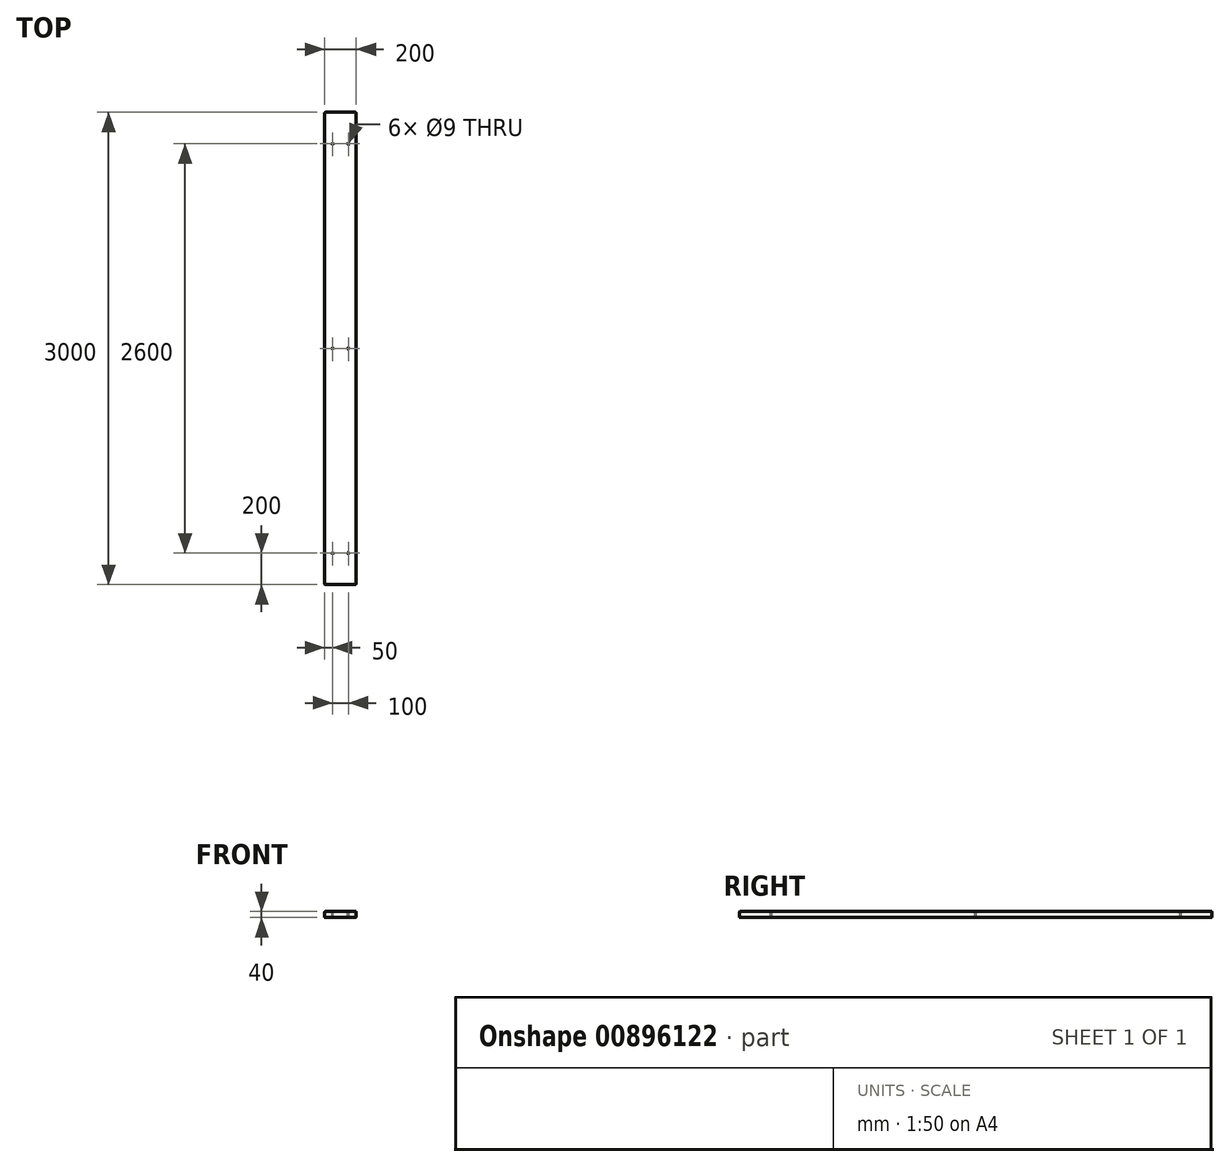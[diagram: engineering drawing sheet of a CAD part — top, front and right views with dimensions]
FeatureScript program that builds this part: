
annotation { "Feature Type Name" : "Feature", "Feature Type Description" : "" }
export const myFeature = defineFeature(function(context is Context, id is Id, definition is map)
    precondition{}
    {
        {
            var Q0;
            Q0=qCreatedBy(makeId("Front.planeOp"),FACE);
            var sketch = newSketch(context, id + "F0", { "sketchPlane" : qUnion([Q0])});
            skLineSegment(sketch, "E0.bottom", {"start": v(0, 0) * mm, "end": v(200, 0) * mm});
            skLineSegment(sketch, "E0.top", {"start": v(0, 40) * mm, "end": v(200, 40) * mm});
            skLineSegment(sketch, "E0.left", {"start": v(0, 0) * mm, "end": v(0, 40) * mm});
            skLineSegment(sketch, "E0.right", {"start": v(200, 0) * mm, "end": v(200, 40) * mm});
            skSolve(sketch);
        }
        {
            var Q0;
            Q0=qSketchRegion(id+"F0",true);
            extrude(context, id + "F1", {"entities" : qUnion([Q0]), "depth" : 3000 * mm, "offsetDistance" : 25 * mm});
        }
        {
            var Q0;
            Q0=makeQuery(id+"F1.opExtrude","SWEPT_FACE",FACE,{"disambiguationData":[OSD([sQuery(id+"F0.wireOp",EDGE,"E0.top")])]});
            var sketch = newSketch(context, id + "F2", { "sketchPlane" : qUnion([Q0])});
            skLineSegment(sketch, "E1", {"start": v(0, -3000) * mm, "end": v(50, -3000) * mm, "construction": true});
            skLineSegment(sketch, "E2", {"start": v(50, -3000) * mm, "end": v(150, -3000) * mm, "construction": true});
            skLineSegment(sketch, "E3", {"start": v(150, -3000) * mm, "end": v(200, -3000) * mm, "construction": true});
            skLineSegment(sketch, "E4", {"start": v(50, -3000) * mm, "end": v(50, -2800) * mm, "construction": true});
            skLineSegment(sketch, "E5", {"start": v(50, -2800) * mm, "end": v(50, -200) * mm, "construction": true});
            skLineSegment(sketch, "E6", {"start": v(50, -200) * mm, "end": v(50, 0) * mm, "construction": true});
            skLineSegment(sketch, "E7", {"start": v(150, -3000) * mm, "end": v(150, -2800) * mm, "construction": true});
            skLineSegment(sketch, "E8", {"start": v(150, -2800) * mm, "end": v(150, -200) * mm, "construction": true});
            skLineSegment(sketch, "E9", {"start": v(150, -200) * mm, "end": v(150, 0) * mm, "construction": true});
            skCircle(sketch, "E10", {"center": v(50, -2800) * mm, "radius": 4.5 * mm});
            skCircle(sketch, "E11", {"center": v(150, -2800) * mm, "radius": 4.5 * mm});
            skCircle(sketch, "E12", {"center": v(50, -200) * mm, "radius": 4.5 * mm});
            skCircle(sketch, "E13", {"center": v(150, -200) * mm, "radius": 4.5 * mm});
            skPoint(sketch, "E14", {"position": v(50, -1500) * mm});
            skPoint(sketch, "E15", {"position": v(150, -1500) * mm});
            skCircle(sketch, "E16", {"center": v(50, -1500) * mm, "radius": 4.5 * mm});
            skCircle(sketch, "E17", {"center": v(150, -1500) * mm, "radius": 4.5 * mm});
            skSolve(sketch);
        }
        {
            var Q0;
            Q0=qSketchRegion(id+"F2",true);
            extrude(context, id + "F3", {"entities" : qUnion([Q0]), "operationType" : NewBodyOperationType.REMOVE, "endBound" : BoundingType.THROUGH_ALL, "oppositeDirection" : true, "depth" : 25 * mm, "offsetDistance" : 25 * mm});
        }
        {
            var Q0;
            Q0=makeQuery(id+"F1.opExtrude","SWEPT_EDGE",EDGE,{"disambiguationData":[OSD([sQuery(id+"F0.wireOp",EDGE,"E0.top"),sQuery(id+"F0.wireOp",EDGE,"E0.left")])]});
            var Q1;
            Q1=makeQuery(id+"F1.opExtrude","SWEPT_EDGE",EDGE,{"disambiguationData":[OSD([sQuery(id+"F0.wireOp",EDGE,"E0.bottom"),sQuery(id+"F0.wireOp",EDGE,"E0.left")])]});
            var Q2;
            Q2=makeQuery(id+"F1.opExtrude","SWEPT_EDGE",EDGE,{"disambiguationData":[OSD([sQuery(id+"F0.wireOp",EDGE,"E0.top"),sQuery(id+"F0.wireOp",EDGE,"E0.right")])]});
            var Q3;
            Q3=makeQuery(id+"F1.opExtrude","SWEPT_EDGE",EDGE,{"disambiguationData":[OSD([sQuery(id+"F0.wireOp",EDGE,"E0.bottom"),sQuery(id+"F0.wireOp",EDGE,"E0.right")])]});
            var Q4;
            Q4=makeQuery(id+"F1.opExtrude","CAP_EDGE",EDGE,{"disambiguationData":[OSD([sQuery(id+"F0.wireOp",EDGE,"E0.top")])],"isStart":false});
            var Q5;
            Q5=makeQuery(id+"F1.opExtrude","CAP_EDGE",EDGE,{"disambiguationData":[OSD([sQuery(id+"F0.wireOp",EDGE,"E0.bottom")])],"isStart":false});
            var Q6;
            Q6=makeQuery(id+"F1.opExtrude","CAP_EDGE",EDGE,{"disambiguationData":[OSD([sQuery(id+"F0.wireOp",EDGE,"E0.left")])],"isStart":false});
            var Q7;
            Q7=makeQuery(id+"F1.opExtrude","CAP_EDGE",EDGE,{"disambiguationData":[OSD([sQuery(id+"F0.wireOp",EDGE,"E0.right")])],"isStart":false});
            var Q8;
            Q8=makeQuery(id+"F1.opExtrude","CAP_EDGE",EDGE,{"disambiguationData":[OSD([sQuery(id+"F0.wireOp",EDGE,"E0.right")])],"isStart":true});
            var Q9;
            Q9=makeQuery(id+"F1.opExtrude","CAP_EDGE",EDGE,{"disambiguationData":[OSD([sQuery(id+"F0.wireOp",EDGE,"E0.top")])],"isStart":true});
            var Q10;
            Q10=makeQuery(id+"F1.opExtrude","CAP_EDGE",EDGE,{"disambiguationData":[OSD([sQuery(id+"F0.wireOp",EDGE,"E0.bottom")])],"isStart":true});
            var Q11;
            Q11=makeQuery(id+"F1.opExtrude","CAP_EDGE",EDGE,{"disambiguationData":[OSD([sQuery(id+"F0.wireOp",EDGE,"E0.left")])],"isStart":true});
            fillet(context, id + "F4", {"entities" : qUnion([Q0, Q1, Q2, Q3, Q4, Q5, Q6, Q7, Q8, Q9, Q10, Q11]), "radius" : 5 * mm, "tangentPropagation" : true, "allowEdgeOverflow" : false});
        }
    });
